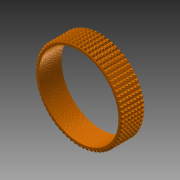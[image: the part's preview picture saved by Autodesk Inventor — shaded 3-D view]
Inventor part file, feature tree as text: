
AUTODESK INVENTOR PART (.ipt)
format: ipt  version: 2014 SP1 (Build 180222100, 222)  size: 4,048,896 bytes
history: native  units: in
note: dims shown in document units (in); Inventor stores cm internally (conversion verified against a paired STEP export)
features: chamfer x2, extrude x1, fillet x1, pattern_circular x1, pattern_linear x1, sketch x1
ambient origin geometry x8: Origin, YZ Plane, XZ Plane, XY Plane, X Axis, Y Axis, Z Axis, Center Point
bodies: Solid1 (feature_tree)
feature tree (7):
  extrude  "Extrusion1"  Depth=0.02in
  chamfer  "Chamfer1"  Distance=3.8in
  chamfer  "Chamfer2"  Distance=0.0375in
  fillet  "Fillet1"  Radius=0.0187in
  pattern_circular  "Circular Pattern1"  [2 undecoded]
  pattern_linear  "Rectangular Pattern1"  Spacing1=0.03in  [1 undecoded]
  sketch  "Sketch1"  dims[d0=4.0in d1=3.6in d2=3.8in d3=0.0375in d4=0.0187in d5=0.06in d6=0.03in d7=0.01in d8=0.1457in d9=0.0in d10=0.09in d11=0.125in d12=0.1718in d13=0.09in d14=0.125in d15=0.1718in d16=0.02in d17=25.9843in d18=360.0deg d20=2.7559in d22=0.1457in]
note: 3 required parameter values undecoded (feature->parameter linkage not recoverable at this tier; creation-order binding heuristic only, values carry confidence <= 0.55)
